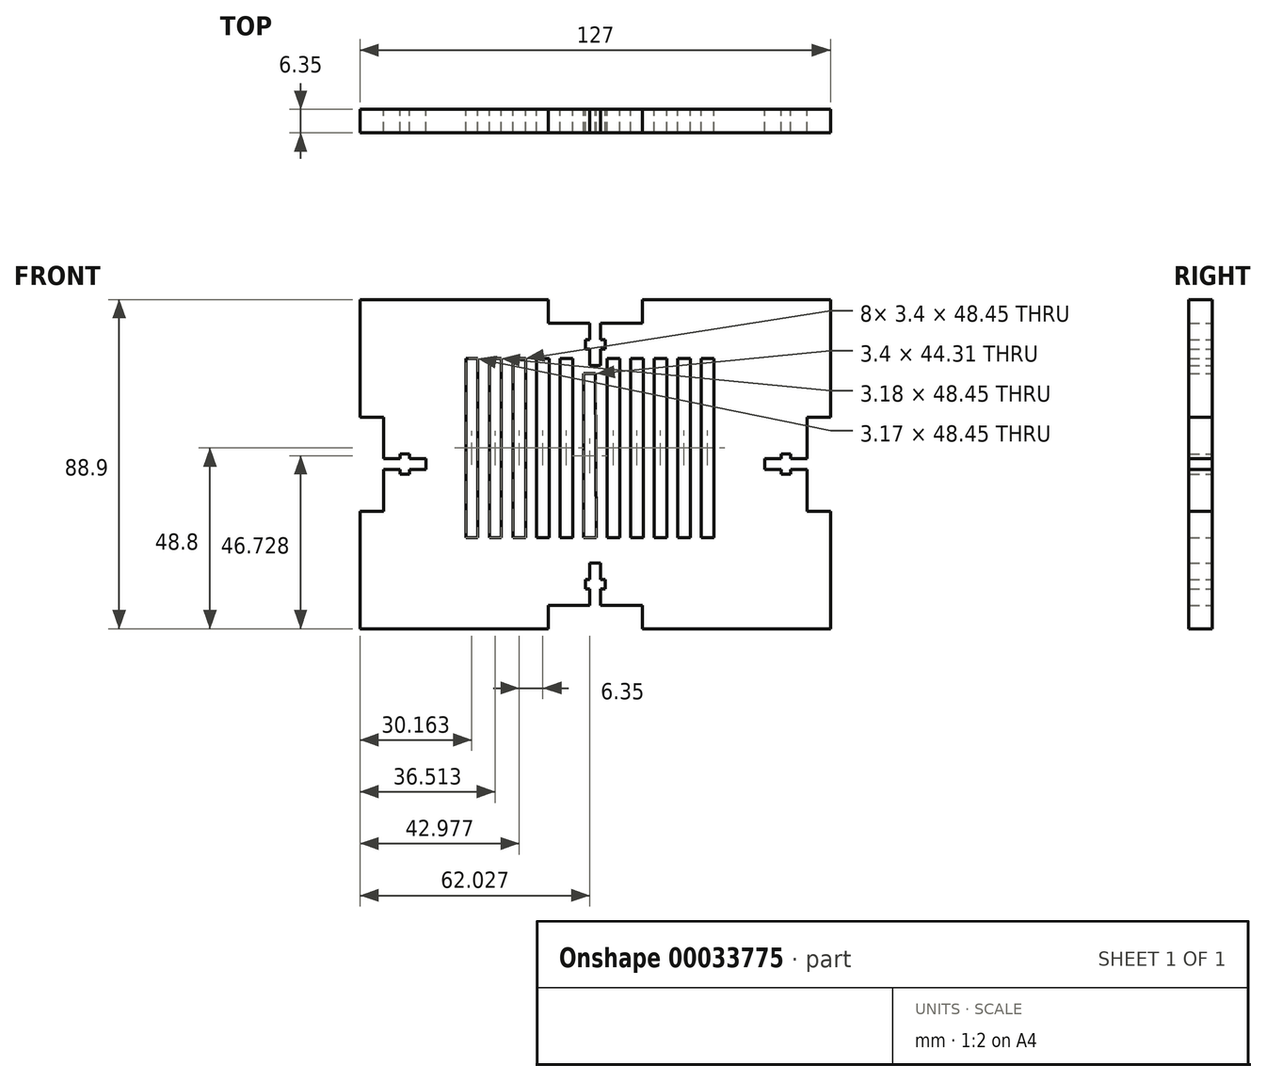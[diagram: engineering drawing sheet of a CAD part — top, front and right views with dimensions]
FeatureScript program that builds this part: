
annotation { "Feature Type Name" : "Feature", "Feature Type Description" : "" }
export const myFeature = defineFeature(function(context is Context, id is Id, definition is map)
    precondition{}
    {
        {
            var Q0;
            Q0=qCreatedBy(makeId("Front.planeOp"),FACE);
            var sketch = newSketch(context, id + "F0", { "sketchPlane" : qUnion([Q0])});
            skLineSegment(sketch, "E0.rect.bottom", {"start": v(57.15, -44.45) * mm, "end": v(12.7, -44.45) * mm});
            skLineSegment(sketch, "E0.rect.top", {"start": v(57.15, 44.45) * mm, "end": v(12.7, 44.45) * mm});
            skPoint(sketch, "E0.rect.middle", {"position": v(0, 0) * mm});
            skLineSegment(sketch, "E1.0", {"start": v(57.15, 38.1) * mm, "end": v(-57.15, 38.1) * mm, "construction": true});
            skLineSegment(sketch, "E1.1", {"start": v(57.15, -38.1) * mm, "end": v(57.15, 38.1) * mm, "construction": true});
            skLineSegment(sketch, "E1.2", {"start": v(57.15, -38.1) * mm, "end": v(-57.15, -38.1) * mm, "construction": true});
            skLineSegment(sketch, "E2", {"start": v(-63.5, 0) * mm, "end": v(-57.15, 0) * mm, "construction": true});
            skLineSegment(sketch, "E3", {"start": v(0, 44.45) * mm, "end": v(0, -44.45) * mm, "construction": true});
            skLineSegment(sketch, "E4.MirrorCS", {"start": v(12.7, 44.45) * mm, "end": v(12.7, -44.45) * mm, "construction": true});
            skLineSegment(sketch, "E5.0", {"start": v(-63.5, -12.7) * mm, "end": v(63.5, -12.7) * mm, "construction": true});
            skLineSegment(sketch, "E6.MirrorCS", {"start": v(-63.5, 12.7) * mm, "end": v(-57.15, 12.7) * mm, "construction": true});
            skLineSegment(sketch, "E7", {"start": v(-63.5, 12.7) * mm, "end": v(-57.15, 12.7) * mm});
            skLineSegment(sketch, "E8", {"start": v(-63.5, -12.7) * mm, "end": v(-57.15, -12.7) * mm});
            skPoint(sketch, "E9.orphan", {"position": v(-63.5, -44.45) * mm});
            skPoint(sketch, "E10.orphan", {"position": v(-63.5, 44.45) * mm});
            skLineSegment(sketch, "E11.MirrorCS", {"start": v(63.5, -12.7) * mm, "end": v(57.15, -12.7) * mm});
            skLineSegment(sketch, "E12.MirrorCS", {"start": v(63.5, 12.7) * mm, "end": v(57.15, 12.7) * mm});
            skPoint(sketch, "E13.orphan", {"position": v(63.5, 44.45) * mm});
            skPoint(sketch, "E14.orphan", {"position": v(63.5, -44.45) * mm});
            skLineSegment(sketch, "E15", {"start": v(-12.7, 44.45) * mm, "end": v(-12.7, 38.1) * mm});
            skLineSegment(sketch, "E16", {"start": v(-12.7, 38.1) * mm, "end": v(-1.46, 38.1) * mm});
            skLineSegment(sketch, "E17", {"start": v(12.7, 38.1) * mm, "end": v(12.7, 44.45) * mm});
            skLineSegment(sketch, "E18.MirrorCS", {"start": v(-12.7, -44.45) * mm, "end": v(-12.7, -38.1) * mm});
            skLineSegment(sketch, "E19.MirrorCS", {"start": v(-12.7, -38.1) * mm, "end": v(-1.46, -38.1) * mm});
            skLineSegment(sketch, "E20.MirrorCS", {"start": v(12.7, -38.1) * mm, "end": v(12.7, -44.45) * mm});
            skLineSegment(sketch, "E21.trimOffspring", {"start": v(-12.7, 44.45) * mm, "end": v(-57.15, 44.45) * mm});
            skLineSegment(sketch, "E22.trimOffspring", {"start": v(-12.7, -44.45) * mm, "end": v(-57.15, -44.45) * mm});
            skLineSegment(sketch, "E23", {"start": v(-12.7, 26.67) * mm, "end": v(12.7, 26.67) * mm, "construction": true});
            skLineSegment(sketch, "E24.0", {"start": v(-1.46, 44.45) * mm, "end": v(-1.46, -44.45) * mm, "construction": true});
            skLineSegment(sketch, "E25.0", {"start": v(-2.7, 44.45) * mm, "end": v(-2.7, -44.45) * mm, "construction": true});
            skLineSegment(sketch, "E26.MirrorCS", {"start": v(1.46, 44.45) * mm, "end": v(1.46, -44.45) * mm, "construction": true});
            skLineSegment(sketch, "E27.MirrorCS", {"start": v(2.7, 44.45) * mm, "end": v(2.7, -44.45) * mm, "construction": true});
            skLineSegment(sketch, "E28", {"start": v(-12.7, 26.67) * mm, "end": v(-12.7, -44.45) * mm, "construction": true});
            skLineSegment(sketch, "E29", {"start": v(-12.7, 38.1) * mm, "end": v(-12.7, 26.67) * mm, "construction": true});
            skLineSegment(sketch, "E30", {"start": v(-12.7, 32.39) * mm, "end": v(12.7, 32.39) * mm, "construction": true});
            skLineSegment(sketch, "E31.0", {"start": v(-12.7, 31.12) * mm, "end": v(12.7, 31.12) * mm, "construction": true});
            skLineSegment(sketch, "E32.MirrorCS", {"start": v(-12.7, 33.66) * mm, "end": v(12.7, 33.66) * mm, "construction": true});
            skLineSegment(sketch, "E33", {"start": v(-1.46, 38.1) * mm, "end": v(-1.46, 33.66) * mm});
            skPoint(sketch, "E33.endSnap0", {"position": v(0, 33.66) * mm});
            skLineSegment(sketch, "E34", {"start": v(-1.46, 33.66) * mm, "end": v(-2.7, 33.66) * mm});
            skLineSegment(sketch, "E35", {"start": v(-2.7, 33.66) * mm, "end": v(-2.7, 31.12) * mm});
            skLineSegment(sketch, "E36", {"start": v(-2.7, 31.12) * mm, "end": v(-1.46, 31.12) * mm});
            skLineSegment(sketch, "E37", {"start": v(-1.46, 31.12) * mm, "end": v(-1.46, 26.67) * mm});
            skLineSegment(sketch, "E38", {"start": v(-1.46, 26.67) * mm, "end": v(1.46, 26.67) * mm});
            skLineSegment(sketch, "E39", {"start": v(1.46, 26.67) * mm, "end": v(1.46, 31.12) * mm});
            skLineSegment(sketch, "E40", {"start": v(1.46, 31.12) * mm, "end": v(2.7, 31.12) * mm});
            skLineSegment(sketch, "E41", {"start": v(2.7, 31.12) * mm, "end": v(2.7, 33.66) * mm});
            skLineSegment(sketch, "E42", {"start": v(2.7, 33.66) * mm, "end": v(1.46, 33.66) * mm});
            skLineSegment(sketch, "E43", {"start": v(1.46, 33.66) * mm, "end": v(1.46, 38.1) * mm});
            skLineSegment(sketch, "E44.trimOffspring", {"start": v(1.46, 38.1) * mm, "end": v(12.7, 38.1) * mm});
            skLineSegment(sketch, "E45.MirrorCS", {"start": v(1.46, -33.66) * mm, "end": v(1.46, -38.1) * mm});
            skLineSegment(sketch, "E46.MirrorCS", {"start": v(2.7, -33.66) * mm, "end": v(1.46, -33.66) * mm});
            skLineSegment(sketch, "E47.MirrorCS", {"start": v(2.7, -31.12) * mm, "end": v(2.7, -33.66) * mm});
            skLineSegment(sketch, "E48.MirrorCS", {"start": v(1.46, -31.12) * mm, "end": v(2.7, -31.12) * mm});
            skLineSegment(sketch, "E49.MirrorCS", {"start": v(1.46, -26.67) * mm, "end": v(1.46, -31.12) * mm});
            skLineSegment(sketch, "E50.MirrorCS", {"start": v(-1.46, -26.67) * mm, "end": v(1.46, -26.67) * mm});
            skLineSegment(sketch, "E51.MirrorCS", {"start": v(-1.46, -31.12) * mm, "end": v(-1.46, -26.67) * mm});
            skLineSegment(sketch, "E52.MirrorCS", {"start": v(-2.7, -31.12) * mm, "end": v(-1.46, -31.12) * mm});
            skLineSegment(sketch, "E53.MirrorCS", {"start": v(-2.7, -33.66) * mm, "end": v(-2.7, -31.12) * mm});
            skLineSegment(sketch, "E54.MirrorCS", {"start": v(-1.46, -33.66) * mm, "end": v(-2.7, -33.66) * mm});
            skLineSegment(sketch, "E55.MirrorCS", {"start": v(-1.46, -38.1) * mm, "end": v(-1.46, -33.66) * mm});
            skLineSegment(sketch, "E56.trimOffspring", {"start": v(1.46, -38.1) * mm, "end": v(12.7, -38.1) * mm});
            skLineSegment(sketch, "E57", {"start": v(-57.15, 0) * mm, "end": v(-57.15, 38.1) * mm, "construction": true});
            skLineSegment(sketch, "E58", {"start": v(-34.93, 0) * mm, "end": v(63.5, 0) * mm, "construction": true});
            skLineSegment(sketch, "E59", {"start": v(-34.93, 44.45) * mm, "end": v(-34.93, -44.45) * mm, "construction": true});
            skLineSegment(sketch, "E60", {"start": v(-34.93, 28.57) * mm, "end": v(-57.15, 28.57) * mm, "construction": true});
            skPoint(sketch, "E60.startSnap0", {"position": v(-57.15, 28.57) * mm});
            skLineSegment(sketch, "E61", {"start": v(-34.93, 28.57) * mm, "end": v(57.15, 28.58) * mm, "construction": true});
            skLineSegment(sketch, "E62", {"start": v(57.15, -28.57) * mm, "end": v(-57.15, -28.58) * mm, "construction": true});
            skPoint(sketch, "E63.rect.middle", {"position": v(34.93, 28.58) * mm});
            skPoint(sketch, "E64.visualSharp", {"position": v(21.6, -12.7) * mm});
            skPoint(sketch, "E65.visualSharp", {"position": v(48.26, -12.7) * mm});
            skPoint(sketch, "E66.visualSharp", {"position": v(48.26, -25.4) * mm});
            skPoint(sketch, "E67.visualSharp", {"position": v(43.18, -31.75) * mm});
            skPoint(sketch, "E68.visualSharp", {"position": v(26.67, -31.75) * mm});
            skPoint(sketch, "E69.visualSharp", {"position": v(21.6, -25.4) * mm});
            skLineSegment(sketch, "E70", {"start": v(21.6, -19.87) * mm, "end": v(-34.93, -19.87) * mm, "construction": true});
            skLineSegment(sketch, "E71", {"start": v(-57.15, 44.45) * mm, "end": v(-63.5, 44.45) * mm});
            skLineSegment(sketch, "E72", {"start": v(-63.5, 12.7) * mm, "end": v(-63.5, 44.45) * mm});
            skLineSegment(sketch, "E73", {"start": v(-63.5, -12.7) * mm, "end": v(-63.5, -44.45) * mm});
            skLineSegment(sketch, "E74", {"start": v(-57.15, -44.45) * mm, "end": v(-63.5, -44.45) * mm});
            skLineSegment(sketch, "E75", {"start": v(57.15, -44.45) * mm, "end": v(63.5, -44.45) * mm});
            skLineSegment(sketch, "E76", {"start": v(63.5, -44.45) * mm, "end": v(63.5, -12.7) * mm});
            skLineSegment(sketch, "E77", {"start": v(63.5, 12.7) * mm, "end": v(63.5, 44.45) * mm});
            skLineSegment(sketch, "E78", {"start": v(63.5, 44.45) * mm, "end": v(57.15, 44.45) * mm});
            skLineSegment(sketch, "E79", {"start": v(-57.15, -12.7) * mm, "end": v(-57.15, -2.7) * mm});
            skPoint(sketch, "E80.center.orphan", {"position": v(-60.33, 0) * mm});
            skLineSegment(sketch, "E81", {"start": v(57.15, 12.7) * mm, "end": v(57.15, 1.46) * mm});
            skPoint(sketch, "E82.MirrorCS.end.orphan", {"position": v(57.15, 12.7) * mm});
            skPoint(sketch, "E82.MirrorCS.start.orphan", {"position": v(50.8, 12.7) * mm});
            skPoint(sketch, "E83.MirrorCS.start.orphan", {"position": v(50.8, -12.7) * mm});
            skPoint(sketch, "E84.orphan", {"position": v(57.15, -12.7) * mm});
            skPoint(sketch, "E85.MirrorCS.end.orphan", {"position": v(63.5, 12.7) * mm});
            skPoint(sketch, "E86.MirrorCS.start.orphan", {"position": v(-50.8, -12.7) * mm});
            skPoint(sketch, "E87.MirrorCS.end.orphan", {"position": v(-57.15, 12.7) * mm});
            skPoint(sketch, "E88.MirrorCS.end.orphan", {"position": v(-57.15, -12.7) * mm});
            skLineSegment(sketch, "E89", {"start": v(-34.93, 0) * mm, "end": v(-57.15, 0) * mm, "construction": true});
            skLineSegment(sketch, "E90.0", {"start": v(-34.93, 1.46) * mm, "end": v(-57.15, 1.46) * mm, "construction": true});
            skLineSegment(sketch, "E91.MirrorCS", {"start": v(-34.93, -1.46) * mm, "end": v(-57.15, -1.46) * mm, "construction": true});
            skLineSegment(sketch, "E92.0", {"start": v(-34.93, 2.7) * mm, "end": v(-57.15, 2.7) * mm, "construction": true});
            skLineSegment(sketch, "E93.MirrorCS", {"start": v(-34.93, -2.7) * mm, "end": v(-57.15, -2.7) * mm, "construction": true});
            skLineSegment(sketch, "E94", {"start": v(-45.72, 12.7) * mm, "end": v(-45.72, -12.7) * mm, "construction": true});
            skLineSegment(sketch, "E95.trimOffspring", {"start": v(-45.72, 12.7) * mm, "end": v(63.5, 12.7) * mm, "construction": true});
            skLineSegment(sketch, "E96", {"start": v(-57.15, 12.7) * mm, "end": v(-45.72, 12.7) * mm, "construction": true});
            skLineSegment(sketch, "E97", {"start": v(-52.7, -1.46) * mm, "end": v(-57.15, -1.46) * mm});
            skLineSegment(sketch, "E98.trimOffspring", {"start": v(-57.15, 1.46) * mm, "end": v(-57.15, 12.7) * mm});
            skLineSegment(sketch, "E99", {"start": v(-57.15, -1.46) * mm, "end": v(-57.15, -2.7) * mm});
            skLineSegment(sketch, "E100.trimOffspring", {"start": v(57.15, -1.46) * mm, "end": v(57.15, -12.7) * mm});
            skLineSegment(sketch, "E101", {"start": v(-51.44, 12.7) * mm, "end": v(-51.44, -12.7) * mm, "construction": true});
            skLineSegment(sketch, "E102.0", {"start": v(-52.7, 12.7) * mm, "end": v(-52.7, -12.7) * mm, "construction": true});
            skLineSegment(sketch, "E103.MirrorCS", {"start": v(-50.17, 12.7) * mm, "end": v(-50.17, -12.7) * mm, "construction": true});
            skLineSegment(sketch, "E104", {"start": v(-57.15, 1.46) * mm, "end": v(-52.7, 1.46) * mm});
            skLineSegment(sketch, "E105", {"start": v(-52.7, 1.46) * mm, "end": v(-52.7, 2.7) * mm});
            skLineSegment(sketch, "E106", {"start": v(-52.7, 2.7) * mm, "end": v(-50.17, 2.7) * mm});
            skLineSegment(sketch, "E107", {"start": v(-50.17, 2.7) * mm, "end": v(-50.17, 1.46) * mm});
            skLineSegment(sketch, "E108", {"start": v(-50.17, 1.46) * mm, "end": v(-45.72, 1.46) * mm});
            skLineSegment(sketch, "E109", {"start": v(-45.72, 1.46) * mm, "end": v(-45.72, -1.46) * mm});
            skLineSegment(sketch, "E110", {"start": v(-45.72, -1.46) * mm, "end": v(-50.17, -1.46) * mm});
            skLineSegment(sketch, "E111", {"start": v(-50.17, -1.46) * mm, "end": v(-50.17, -2.7) * mm});
            skLineSegment(sketch, "E112", {"start": v(-50.17, -2.7) * mm, "end": v(-52.7, -2.7) * mm});
            skLineSegment(sketch, "E113", {"start": v(-52.7, -2.7) * mm, "end": v(-52.7, -1.46) * mm});
            skLineSegment(sketch, "E114.MirrorCS", {"start": v(52.7, -1.46) * mm, "end": v(57.15, -1.46) * mm});
            skLineSegment(sketch, "E115.MirrorCS", {"start": v(52.7, -2.7) * mm, "end": v(52.7, -1.46) * mm});
            skLineSegment(sketch, "E116.MirrorCS", {"start": v(50.17, -2.7) * mm, "end": v(52.7, -2.7) * mm});
            skLineSegment(sketch, "E117.MirrorCS", {"start": v(50.17, -1.46) * mm, "end": v(50.17, -2.7) * mm});
            skLineSegment(sketch, "E118.MirrorCS", {"start": v(45.72, -1.46) * mm, "end": v(50.17, -1.46) * mm});
            skLineSegment(sketch, "E119.MirrorCS", {"start": v(45.72, 1.46) * mm, "end": v(45.72, -1.46) * mm});
            skLineSegment(sketch, "E120.MirrorCS", {"start": v(50.17, 1.46) * mm, "end": v(45.72, 1.46) * mm});
            skLineSegment(sketch, "E121.MirrorCS", {"start": v(50.17, 2.7) * mm, "end": v(50.17, 1.46) * mm});
            skLineSegment(sketch, "E122.MirrorCS", {"start": v(52.7, 2.7) * mm, "end": v(50.17, 2.7) * mm});
            skLineSegment(sketch, "E123.MirrorCS", {"start": v(52.7, 1.46) * mm, "end": v(52.7, 2.7) * mm});
            skLineSegment(sketch, "E124.MirrorCS", {"start": v(57.15, 1.46) * mm, "end": v(52.7, 1.46) * mm});
            skLineSegment(sketch, "E125", {"start": v(34.93, 44.45) * mm, "end": v(34.93, -19.87) * mm, "construction": true});
            skLineSegment(sketch, "E126.bottom", {"start": v(-34.93, 28.57) * mm, "end": v(-31.75, 28.57) * mm});
            skLineSegment(sketch, "E126.top", {"start": v(-34.93, -19.87) * mm, "end": v(-31.75, -19.87) * mm});
            skLineSegment(sketch, "E126.left", {"start": v(-34.93, 28.57) * mm, "end": v(-34.93, -19.87) * mm});
            skLineSegment(sketch, "E126.right", {"start": v(-31.75, 28.57) * mm, "end": v(-31.75, -19.87) * mm});
            skLineSegment(sketch, "E127.0", {"start": v(-28.58, 28.57) * mm, "end": v(-28.58, -19.87) * mm, "construction": true});
            skLineSegment(sketch, "E128.bottom", {"start": v(-28.58, 28.57) * mm, "end": v(-25.4, 28.57) * mm});
            skLineSegment(sketch, "E128.top", {"start": v(-28.58, -19.87) * mm, "end": v(-25.4, -19.87) * mm});
            skLineSegment(sketch, "E128.left", {"start": v(-28.58, 28.57) * mm, "end": v(-28.58, -19.87) * mm});
            skLineSegment(sketch, "E128.right", {"start": v(-25.4, 28.57) * mm, "end": v(-25.4, -19.87) * mm});
            skLineSegment(sketch, "E129.0", {"start": v(-22.23, 28.57) * mm, "end": v(-22.23, -19.87) * mm, "construction": true});
            skLineSegment(sketch, "E130.bottom", {"start": v(-22.23, 28.57) * mm, "end": v(-18.82, 28.57) * mm});
            skLineSegment(sketch, "E130.top", {"start": v(-22.23, -19.87) * mm, "end": v(-18.82, -19.87) * mm});
            skLineSegment(sketch, "E130.left", {"start": v(-22.23, 28.57) * mm, "end": v(-22.23, -19.87) * mm});
            skLineSegment(sketch, "E130.right", {"start": v(-18.82, 28.57) * mm, "end": v(-18.82, -19.87) * mm});
            skLineSegment(sketch, "E131.1.0.0", {"start": v(-15.88, 28.57) * mm, "end": v(-12.47, 28.57) * mm});
            skLineSegment(sketch, "E131.1.0.1", {"start": v(-15.88, 28.57) * mm, "end": v(-15.88, -19.87) * mm});
            skLineSegment(sketch, "E131.1.0.2", {"start": v(-12.47, 28.57) * mm, "end": v(-12.47, -19.87) * mm});
            skLineSegment(sketch, "E131.1.0.3", {"start": v(-15.88, -19.87) * mm, "end": v(-12.47, -19.87) * mm});
            skLineSegment(sketch, "E131.2.0.0", {"start": v(-9.53, 28.57) * mm, "end": v(-6.12, 28.57) * mm});
            skLineSegment(sketch, "E131.2.0.1", {"start": v(-9.53, 28.57) * mm, "end": v(-9.53, -19.87) * mm});
            skLineSegment(sketch, "E131.2.0.2", {"start": v(-6.12, 28.57) * mm, "end": v(-6.12, -19.87) * mm});
            skLineSegment(sketch, "E131.2.0.3", {"start": v(-9.53, -19.87) * mm, "end": v(-6.12, -19.87) * mm});
            skLineSegment(sketch, "E131.3.0.3", {"start": v(-3.18, -19.87) * mm, "end": v(0.23, -19.87) * mm});
            skLineSegment(sketch, "E131.4.0.0", {"start": v(3.17, 28.57) * mm, "end": v(6.58, 28.57) * mm});
            skLineSegment(sketch, "E131.4.0.1", {"start": v(3.17, 28.57) * mm, "end": v(3.17, -19.87) * mm});
            skLineSegment(sketch, "E131.4.0.2", {"start": v(6.58, 28.57) * mm, "end": v(6.58, -19.87) * mm});
            skLineSegment(sketch, "E131.4.0.3", {"start": v(3.17, -19.87) * mm, "end": v(6.58, -19.87) * mm});
            skLineSegment(sketch, "E131.5.0.0", {"start": v(9.52, 28.57) * mm, "end": v(12.93, 28.57) * mm});
            skLineSegment(sketch, "E131.5.0.1", {"start": v(9.52, 28.57) * mm, "end": v(9.52, -19.87) * mm});
            skLineSegment(sketch, "E131.5.0.2", {"start": v(12.93, 28.57) * mm, "end": v(12.93, -19.87) * mm});
            skLineSegment(sketch, "E131.5.0.3", {"start": v(9.52, -19.87) * mm, "end": v(12.93, -19.87) * mm});
            skLineSegment(sketch, "E131.6.0.0", {"start": v(15.87, 28.57) * mm, "end": v(19.28, 28.57) * mm});
            skLineSegment(sketch, "E131.6.0.1", {"start": v(15.87, 28.57) * mm, "end": v(15.87, -19.87) * mm});
            skLineSegment(sketch, "E131.6.0.2", {"start": v(19.28, 28.57) * mm, "end": v(19.28, -19.87) * mm});
            skLineSegment(sketch, "E131.6.0.3", {"start": v(15.87, -19.87) * mm, "end": v(19.28, -19.87) * mm});
            skLineSegment(sketch, "E131.7.0.0", {"start": v(22.22, 28.57) * mm, "end": v(25.63, 28.57) * mm});
            skLineSegment(sketch, "E131.7.0.1", {"start": v(22.22, 28.57) * mm, "end": v(22.22, -19.87) * mm});
            skLineSegment(sketch, "E131.7.0.2", {"start": v(25.63, 28.57) * mm, "end": v(25.63, -19.87) * mm});
            skLineSegment(sketch, "E131.7.0.3", {"start": v(22.22, -19.87) * mm, "end": v(25.63, -19.87) * mm});
            skLineSegment(sketch, "E131.8.0.0", {"start": v(28.57, 28.57) * mm, "end": v(31.98, 28.57) * mm});
            skLineSegment(sketch, "E131.8.0.1", {"start": v(28.57, 28.57) * mm, "end": v(28.57, -19.87) * mm});
            skLineSegment(sketch, "E131.8.0.2", {"start": v(31.98, 28.57) * mm, "end": v(31.98, -19.87) * mm});
            skLineSegment(sketch, "E131.8.0.3", {"start": v(28.57, -19.87) * mm, "end": v(31.98, -19.87) * mm});
            skLineSegment(sketch, "E131.direction1", {"start": v(-22.23, 28.57) * mm, "end": v(-15.88, 28.57) * mm, "construction": true});
            skLineSegment(sketch, "E132", {"start": v(0.23, -19.87) * mm, "end": v(0, 24.43) * mm});
            skLineSegment(sketch, "E133", {"start": v(0, 24.43) * mm, "end": v(-3.18, 24.43) * mm});
            skLineSegment(sketch, "E134", {"start": v(-3.18, 24.43) * mm, "end": v(-3.18, -19.87) * mm});
            skSolve(sketch);
        }
        {
            var Q0;
            Q0=qSketchRegion(id+"F0",true);
            var Q1;
            Q1=makeQuery(id+"F0.imprint","IMPRINT",FACE,{"disambiguationData":[TD([[makeQuery(id+"F0.imprint","IMPRINT",EDGE,{"derivedFrom":sQuery(id+"F0.wireOp",EDGE,"E0.rect.right")}),-1.0]])]});
            extrude(context, id + "F1", {"entities" : qUnion([Q0, Q1]), "depth" : 6.35 * mm});
        }
    });
